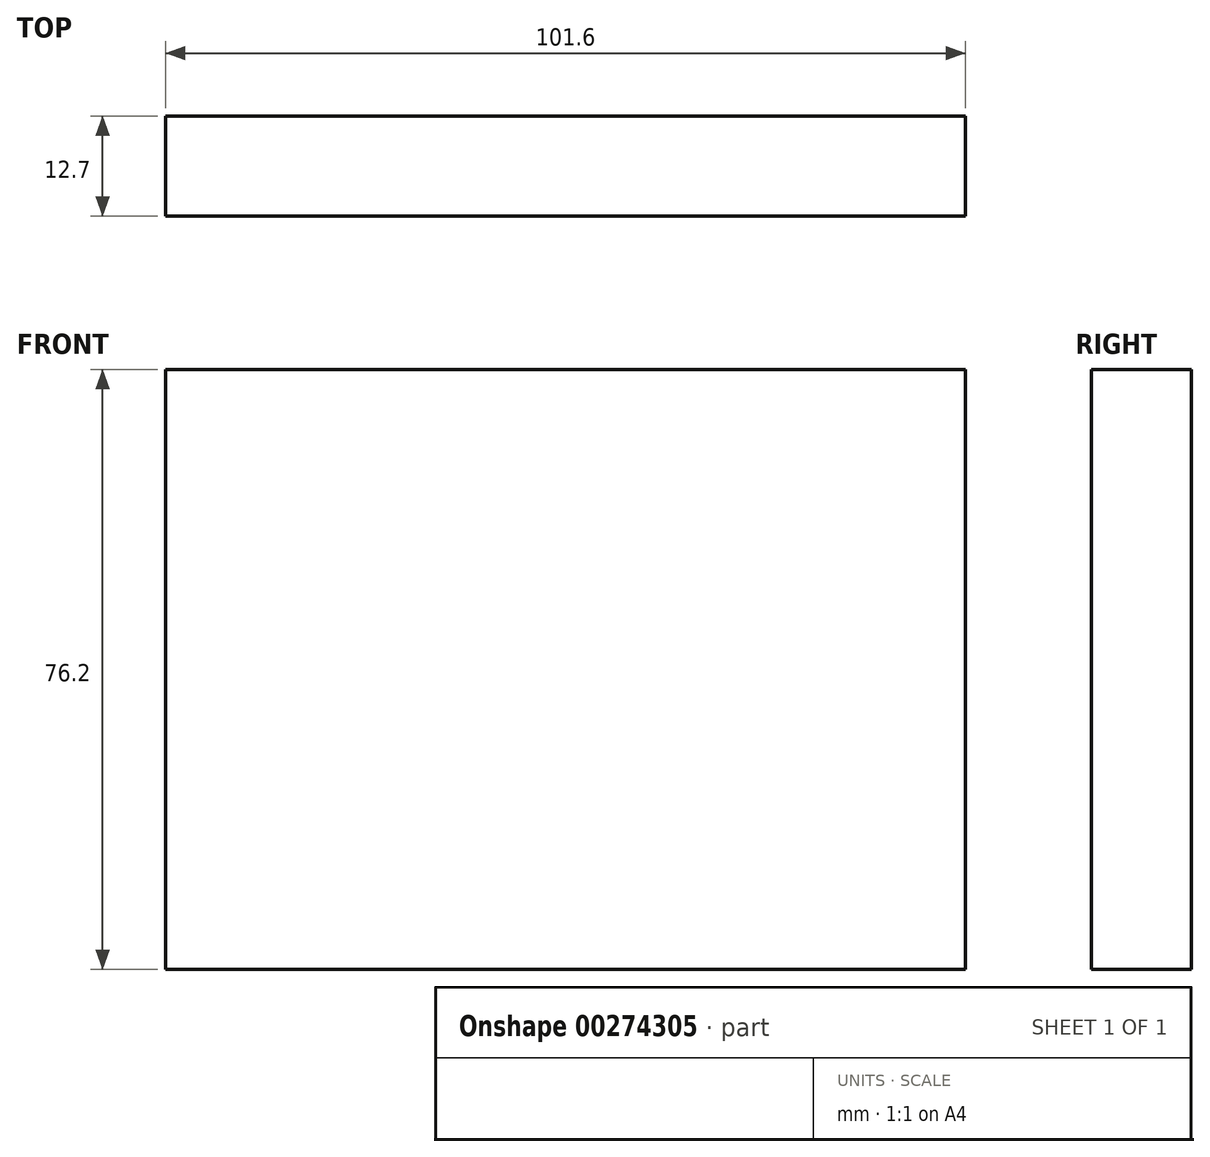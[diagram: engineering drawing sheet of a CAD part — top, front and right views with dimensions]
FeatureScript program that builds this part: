
annotation { "Feature Type Name" : "Feature", "Feature Type Description" : "" }
export const myFeature = defineFeature(function(context is Context, id is Id, definition is map)
    precondition{}
    {
        {
            var Q0;
            Q0=qCreatedBy(makeId("Front.planeOp"),FACE);
            var sketch = newSketch(context, id + "F0", { "sketchPlane" : qUnion([Q0])});
            skLineSegment(sketch, "E0.bottom", {"start": v(0, 0) * mm, "end": v(-101.6, 0) * mm});
            skLineSegment(sketch, "E0.top", {"start": v(0, 76.2) * mm, "end": v(-101.6, 76.2) * mm});
            skLineSegment(sketch, "E0.left", {"start": v(0, 0) * mm, "end": v(0, 76.2) * mm});
            skLineSegment(sketch, "E0.right", {"start": v(-101.6, 0) * mm, "end": v(-101.6, 76.2) * mm});
            skSolve(sketch);
        }
        {
            var Q0;
            Q0 = qSketchRegion(id + "F0", true);
            extrude(context, id + "F1", {"entities" : qUnion([Q0]), "depth" : 12.7 * mm});
        }
        {
            var Q0;
            Q0=makeQuery(id+"F0.imprint","IMPRINT",FACE,{"disambiguationData":[TD([[makeQuery(id+"F0.imprint","IMPRINT",EDGE,{"derivedFrom":sQuery(id+"F0.wireOp",EDGE,"E0.bottom")}),-1.0]])]});
            var sketch = newSketch(context, id + "F2", { "sketchPlane" : qUnion([Q0])});
            skArc(sketch, "E1", {"start": v(0, 76.2) * mm, "mid": v(-53.88, 53.88) * mm, "end": v(-76.2, 0) * mm});
            skSolve(sketch);
        }
        {
            var Q0;
            Q0=qCreatedBy(makeId("Top.planeOp"),FACE);
            var sketch = newSketch(context, id + "F3", { "sketchPlane" : qUnion([Q0])});
            skArc(sketch, "E2", {"start": v(-59, 0) * mm, "mid": v(-76.61, 12.18) * mm, "end": v(-94.22, 0) * mm});
            skSolve(sketch);
        }
    });
